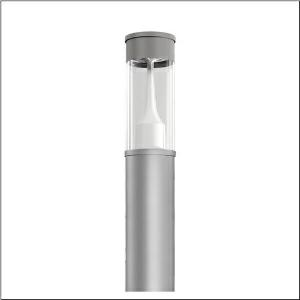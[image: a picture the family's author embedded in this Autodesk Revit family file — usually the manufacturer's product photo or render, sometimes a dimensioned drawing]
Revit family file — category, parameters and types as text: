
# Revit family: city-light_400_iq___p1_0a_5xa5305ff14hp_6c14
name_source: partatom
category: Lighting Fixtures
units: mm (PartAtom-declared; Revit-internal decimal feet)

## family parameters
Cut with Voids When Loaded = No
Host = Face
Light Source = No
Part Type = Normal
Room Calculation Point = No
Round Connector Dimension = Use Diameter
Shared = No

## types (1)
- --- (1 x LED, 4700 lm, 33.6 W, 3000K)
    Apparent Load = 34 VA
    CIE Flux Codes = 31 62 91 95 100
    Color Rendering = 70
    Color Temperature = 3000K
    Default Elevation = 1800 mm
    Description = City-Light 400 iQ, light pillar, Module 540 iQ-SR, primary light control with 3 zone facetted reflector, of plastic, silver coated, highly specular, structured, primary optical cover: cover, of PMMA, transparent, partly coated, light distribution: P1.0a, primary light characteristic: strongly asymmetric, LED, High Power LED, rated luminous flux: 4.700lm, luminous efficacy: 140lm/W, light colour: 730, colour temperature: 3000K, control gear: iQ Street-Remote, control: pre-setting: logarithmic dimming characteristic, Street-Remote, Auto-Match, Temp-Guard, Lumen-Switch, Night-Set, Smart-Wire, Light-Fading, Desk-Remote (wireless, voltage-free reading and setting of iQ features in the workshop via application-optimized NFC function/RFID function), optimised constant luminous flux control (CLO 2.0), with terminal, 6-pole, max. 2.5mm², mains connection: 230..240V, AC, 50/60Hz, start of lifetime: 34W, end of service life: 36W, reduction: 15W, luminaire housing, cylindrical, of extruded aluminium section, coated, Siteco® metallic grey (DB 702S), length: 4.694mm, diameter: 200mm, Module 540 iQ-SR, traffic white (RAL 9016), equipment: Power, protection rating (complete): IP65, insulation class (complete): insulation class II (safety insulation), certification: CE, ENEC, VDE, packaging unit: 1 piece

Light Distribution: P1.0a
    Height = 500 mm
    Lamp = 1 x LED
    Lamp Light Flux = 4700 lm
    Lamp Power = 33.6 W
    Lamp count = 1
    Length = 200 mm  [stored 0.656168 ft]
    Luminous efficacy = 140 lm/W
    Manufacturer = Siteco
    ModVariant = No
    Model = 5XA5305FF14HP
    Mounting Place = Floor
    Mounting Type = Freestanding
    Number of Poles = 1
    OnlyDefault = Yes
    Power Factor = 1
    Product Name = City-Light 400 iQ | P1.0a
    Product group = light pillar
    ProductGroupID = 1301
    Protection Class = Protection class II
    Protection Degree = IP 65
    RLX_Detail_Level = 1
    RLX_Emergency_Light_Flux = 0 lm
    RLX_Emergency_Type = 0
    RLX_Emergency_Type_DB = No
    RlxData = <blob elided: 53241 chars, md5=e894454e>
    Socket = socket
    Standby Power = 0 W
    System Light Flux = 4700 lm
    System Power = 34 W
    Type Comments = factory setting: luminous flux: 100 % | dim-lin: 254 | 695 mA
    Type Image = l_1006916.jpg
    URL = http://relux.com
    VarID = @adj_191767
    Voltage = 0 V
    Weight = 0.00 kg
    Width = 0 mm  [stored 0 ft]

note: [stored X ft] marks values corroborated as IEEE doubles in the binary element streams (Revit-internal decimal feet)

## geometry (parser evidence)
native form markers: Blend x4, Sweep x9
no freeform markers — native parametric forms only
